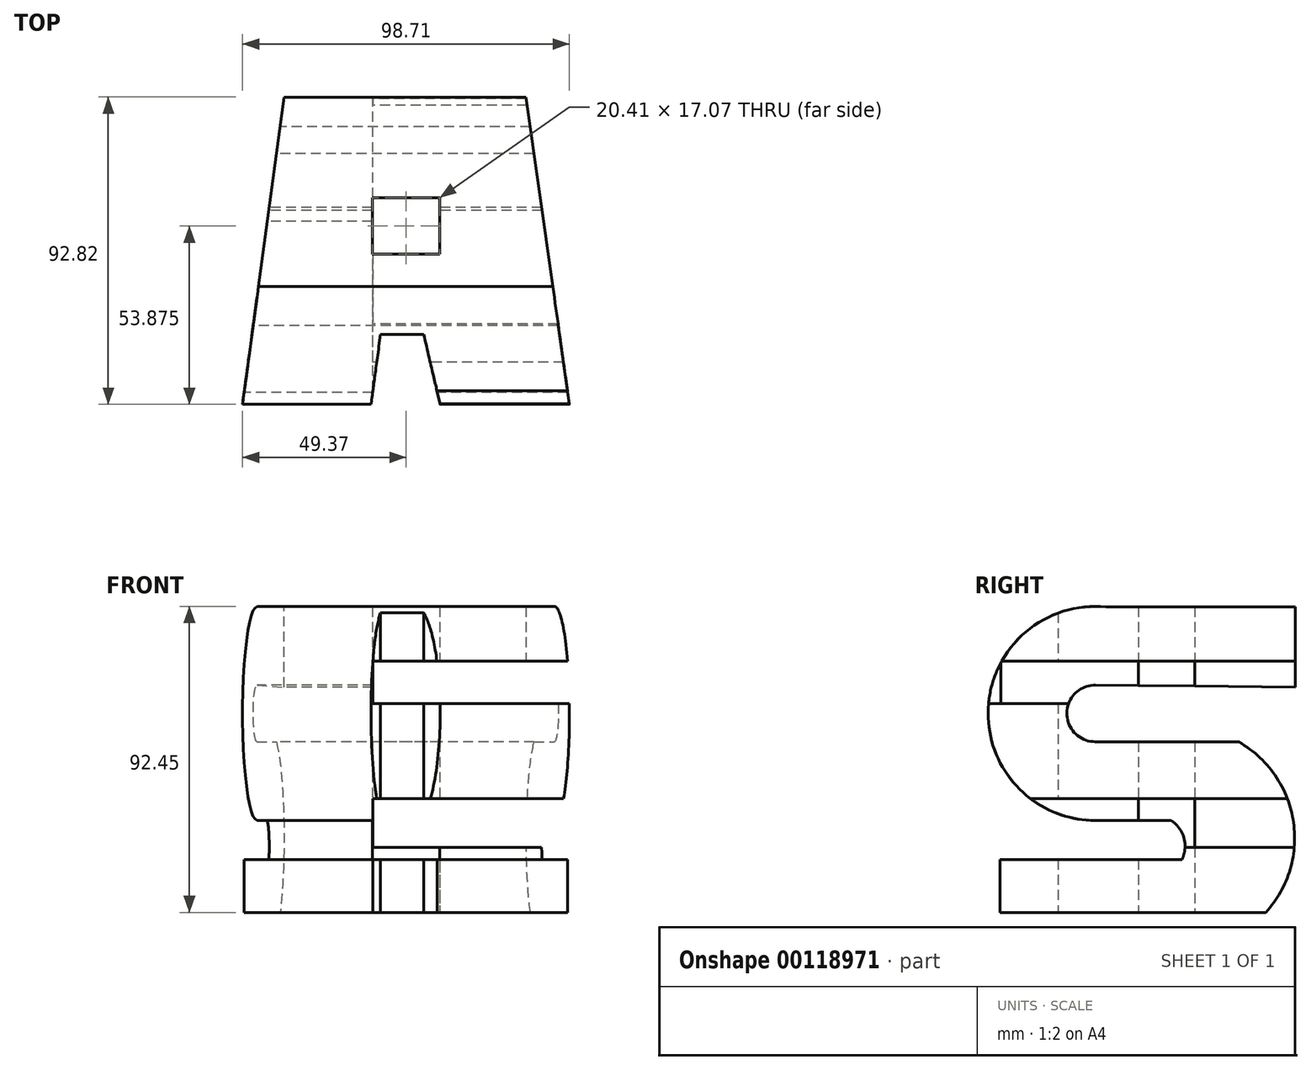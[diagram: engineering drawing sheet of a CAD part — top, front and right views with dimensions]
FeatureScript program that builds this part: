
annotation { "Feature Type Name" : "Feature", "Feature Type Description" : "" }
export const myFeature = defineFeature(function(context is Context, id is Id, definition is map)
    precondition{}
    {
        {
            var Q0;
            Q0=qCreatedBy(makeId("Top.planeOp"),FACE);
            var sketch = newSketch(context, id + "F0", { "sketchPlane" : qUnion([Q0])});
            skLineSegment(sketch, "E0.bottom", {"start": v(50, 50) * mm, "end": v(-50, 50) * mm, "construction": true});
            skLineSegment(sketch, "E0.top", {"start": v(50, -50) * mm, "end": v(-50, -50) * mm, "construction": true});
            skLineSegment(sketch, "E0.left", {"start": v(50, 50) * mm, "end": v(50, -50) * mm, "construction": true});
            skLineSegment(sketch, "E0.right", {"start": v(-50, 50) * mm, "end": v(-50, -50) * mm, "construction": true});
            skPoint(sketch, "E0.middle", {"position": v(0, 0) * mm});
            skLineSegment(sketch, "E1", {"start": v(-50, -50) * mm, "end": v(-36.43, 50) * mm});
            skLineSegment(sketch, "E2", {"start": v(-36.43, 50) * mm, "end": v(35.9, 50) * mm});
            skLineSegment(sketch, "E3", {"start": v(35.9, 50) * mm, "end": v(50, -50) * mm});
            skLineSegment(sketch, "E4.bottom", {"start": v(10.2, 17.07) * mm, "end": v(-10.2, 17.07) * mm});
            skLineSegment(sketch, "E4.top", {"start": v(10.2, 0) * mm, "end": v(-10.2, 0) * mm});
            skLineSegment(sketch, "E4.left", {"start": v(10.2, 17.07) * mm, "end": v(10.2, 0) * mm});
            skLineSegment(sketch, "E4.right", {"start": v(-10.2, 17.07) * mm, "end": v(-10.2, 0) * mm});
            skPoint(sketch, "E4.middle", {"position": v(0, 8.53) * mm});
            skLineSegment(sketch, "E5", {"start": v(-7.7, -24.18) * mm, "end": v(-11.2, -50) * mm});
            skLineSegment(sketch, "E6", {"start": v(-7.7, -24.18) * mm, "end": v(5.35, -24.18) * mm});
            skLineSegment(sketch, "E7", {"start": v(5.35, -24.18) * mm, "end": v(11.4, -50) * mm});
            skLineSegment(sketch, "E8", {"start": v(-50, -50) * mm, "end": v(-11.2, -50) * mm});
            skLineSegment(sketch, "E9.trimOffspring", {"start": v(11.4, -50) * mm, "end": v(50, -50) * mm});
            skLineSegment(sketch, "E10", {"start": v(-50, -10.23) * mm, "end": v(50, -10.23) * mm, "construction": true});
            skLineSegment(sketch, "E11", {"start": v(-50, -24.18) * mm, "end": v(50, -24.18) * mm, "construction": true});
            skLineSegment(sketch, "E12", {"start": v(-50, -31.45) * mm, "end": v(50, -31.45) * mm, "construction": true});
            skLineSegment(sketch, "E13", {"start": v(-50, -40.35) * mm, "end": v(50, -40.35) * mm, "construction": true});
            skLineSegment(sketch, "E14", {"start": v(0, 50) * mm, "end": v(-0.26, -50) * mm, "construction": true});
            skPoint(sketch, "E14.endSnap0", {"position": v(-0.26, 50) * mm});
            skSolve(sketch);
        }
        {
            var Q0;
            Q0=qCreatedBy(makeId("Front.planeOp"),FACE);
            var sketch = newSketch(context, id + "F1", { "sketchPlane" : qUnion([Q0])});
            skLineSegment(sketch, "E15.bottom", {"start": v(-50, 50) * mm, "end": v(50, 50) * mm, "construction": true});
            skLineSegment(sketch, "E15.top", {"start": v(-50, -50) * mm, "end": v(50, -50) * mm, "construction": true});
            skLineSegment(sketch, "E15.left", {"start": v(-50, 50) * mm, "end": v(-50, -50) * mm, "construction": true});
            skLineSegment(sketch, "E15.right", {"start": v(50, 50) * mm, "end": v(50, -50) * mm, "construction": true});
            skPoint(sketch, "E15.middle", {"position": v(0, 0) * mm});
            skLineSegment(sketch, "E16", {"start": v(-50, 50) * mm, "end": v(-50, -50) * mm});
            skLineSegment(sketch, "E17", {"start": v(-50, -50) * mm, "end": v(50, -50) * mm});
            skLineSegment(sketch, "E18", {"start": v(-50, 50) * mm, "end": v(50, 50) * mm});
            skLineSegment(sketch, "E19", {"start": v(-50, 15.16) * mm, "end": v(-10.04, 15.16) * mm, "construction": true});
            skLineSegment(sketch, "E20", {"start": v(-50, -28.3) * mm, "end": v(50, -28.3) * mm, "construction": true});
            skLineSegment(sketch, "E21", {"start": v(-10.04, 50) * mm, "end": v(-10.04, 0) * mm, "construction": true});
            skPoint(sketch, "E21.endSnap0", {"position": v(50, 0) * mm});
            skLineSegment(sketch, "E22", {"start": v(-50, -13.48) * mm, "end": v(50, -13.48) * mm, "construction": true});
            skLineSegment(sketch, "E23", {"start": v(-50, 28.02) * mm, "end": v(-10.04, 28.02) * mm});
            skLineSegment(sketch, "E24", {"start": v(0, 15.16) * mm, "end": v(50, 15.16) * mm});
            skLineSegment(sketch, "E25", {"start": v(0, 28.02) * mm, "end": v(50, 28.02) * mm});
            skLineSegment(sketch, "E26", {"start": v(0, -13.48) * mm, "end": v(50, -13.48) * mm});
            skLineSegment(sketch, "E27", {"start": v(0, -28.3) * mm, "end": v(50, -28.3) * mm});
            skLineSegment(sketch, "E28", {"start": v(50, 28.02) * mm, "end": v(50, 50) * mm});
            skLineSegment(sketch, "E29", {"start": v(50, 50) * mm, "end": v(-50, 50) * mm});
            skLineSegment(sketch, "E30", {"start": v(-50, 28.02) * mm, "end": v(-50, 0) * mm});
            skLineSegment(sketch, "E31", {"start": v(-50, 0) * mm, "end": v(-50, -13.48) * mm});
            skLineSegment(sketch, "E32", {"start": v(-50, -28.3) * mm, "end": v(-50, -50) * mm});
            skLineSegment(sketch, "E33", {"start": v(-50, -13.48) * mm, "end": v(-50, -28.3) * mm});
            skLineSegment(sketch, "E34", {"start": v(-50, 15.16) * mm, "end": v(-50, -13.48) * mm});
            skLineSegment(sketch, "E35", {"start": v(-50, 28.02) * mm, "end": v(-50, 15.16) * mm});
            skLineSegment(sketch, "E36", {"start": v(50, 15.16) * mm, "end": v(-50, 15.16) * mm});
            skLineSegment(sketch, "E37", {"start": v(50, 15.16) * mm, "end": v(50, -13.48) * mm});
            skLineSegment(sketch, "E38", {"start": v(50, 0) * mm, "end": v(-50, 0) * mm});
            skLineSegment(sketch, "E39", {"start": v(0, -13.48) * mm, "end": v(-50, -13.48) * mm});
            skLineSegment(sketch, "E40", {"start": v(0, -28.3) * mm, "end": v(-50, -28.3) * mm});
            skLineSegment(sketch, "E41", {"start": v(50, -28.3) * mm, "end": v(50, -50) * mm});
            skLineSegment(sketch, "E42", {"start": v(0, 50) * mm, "end": v(0, 28.02) * mm});
            skLineSegment(sketch, "E43.trimOffspring", {"start": v(0, 15.16) * mm, "end": v(50, 15.16) * mm, "construction": true});
            skLineSegment(sketch, "E44.trimOffspring", {"start": v(0, 15.16) * mm, "end": v(0, -13.48) * mm});
            skLineSegment(sketch, "E45", {"start": v(-10.04, 50) * mm, "end": v(-10.04, 15.16) * mm});
            skLineSegment(sketch, "E46", {"start": v(-10.04, 28.02) * mm, "end": v(0, 28.02) * mm});
            skLineSegment(sketch, "E47", {"start": v(-10.04, 15.16) * mm, "end": v(-10.04, -28.3) * mm});
            skLineSegment(sketch, "E48.trimOffspring", {"start": v(0, -28.3) * mm, "end": v(0, -50) * mm});
            skSolve(sketch);
        }
        {
            var Q0;
            Q0=qCreatedBy(makeId("Right.planeOp"),FACE);
            var sketch = newSketch(context, id + "F2", { "sketchPlane" : qUnion([Q0])});
            skArc(sketch, "E49", {"start": v(-12.91, 20.78) * mm, "mid": v(-21.57, 12.27) * mm, "end": v(-13.02, 3.65) * mm});
            skLineSegment(sketch, "E50", {"start": v(-13.02, 3.65) * mm, "end": v(30.4, 3.58) * mm});
            skLineSegment(sketch, "E51", {"start": v(-12.91, 20.78) * mm, "end": v(47.48, 20.13) * mm});
            skLineSegment(sketch, "E52", {"start": v(47.48, 20.13) * mm, "end": v(47.48, 44.4) * mm});
            skLineSegment(sketch, "E53", {"start": v(47.48, 44.4) * mm, "end": v(-9.77, 44.4) * mm});
            skArc(sketch, "E54", {"start": v(-9.77, 44.4) * mm, "mid": v(-45.3, 13.84) * mm, "end": v(-13, -20.13) * mm});
            skLineSegment(sketch, "E55", {"start": v(33.8, -47.89) * mm, "end": v(-41.73, -47.89) * mm});
            skLineSegment(sketch, "E56", {"start": v(-41.73, -47.89) * mm, "end": v(-41.73, -31.94) * mm});
            skLineSegment(sketch, "E57", {"start": v(-41.73, -31.94) * mm, "end": v(9.74, -31.94) * mm});
            skArc(sketch, "E58", {"start": v(30.4, 3.58) * mm, "mid": v(46.8, -20.2) * mm, "end": v(38.53, -47.89) * mm});
            skLineSegment(sketch, "E59", {"start": v(-13, -20.13) * mm, "end": v(9.95, -20.13) * mm});
            skArc(sketch, "E60", {"start": v(9.95, -20.13) * mm, "mid": v(13.78, -25.42) * mm, "end": v(13.2, -31.94) * mm});
            skLineSegment(sketch, "E61", {"start": v(33.8, -47.89) * mm, "end": v(38.53, -47.89) * mm});
            skLineSegment(sketch, "E62", {"start": v(9.74, -31.94) * mm, "end": v(13.2, -31.94) * mm});
            skSolve(sketch);
        }
        {
            var Q0;
            Q0 = qSketchRegion(id + "F0", true);
            extrude(context, id + "F3", {"entities" : qUnion([Q0]), "endBound" : BoundingType.SYMMETRIC, "depth" : 100 * mm});
        }
        {
            var Q0;
            Q0 = qSketchRegion(id + "F1", true);
            extrude(context, id + "F4", {"entities" : qUnion([Q0]), "operationType" : NewBodyOperationType.INTERSECT, "endBound" : BoundingType.SYMMETRIC, "depth" : 100 * mm});
        }
        {
            var Q0;
            Q0 = qSketchRegion(id + "F2", true);
            extrude(context, id + "F5", {"entities" : qUnion([Q0]), "operationType" : NewBodyOperationType.INTERSECT, "endBound" : BoundingType.SYMMETRIC, "depth" : 100 * mm});
        }
    });
